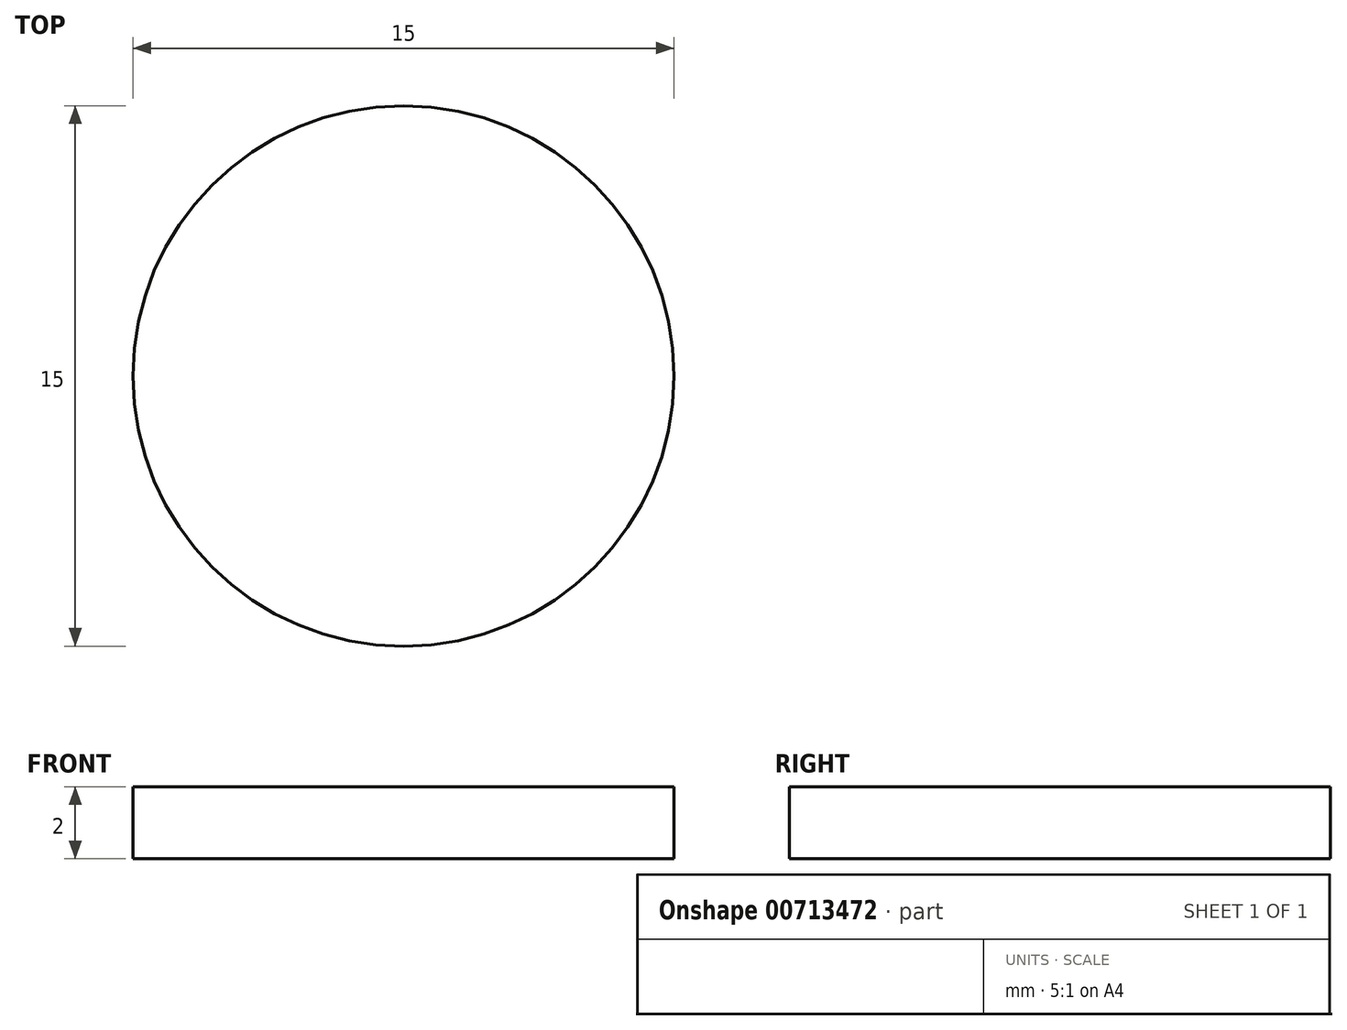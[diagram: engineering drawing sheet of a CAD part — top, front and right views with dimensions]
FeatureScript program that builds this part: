
annotation { "Feature Type Name" : "Feature", "Feature Type Description" : "" }
export const myFeature = defineFeature(function(context is Context, id is Id, definition is map)
    precondition{}
    {
        {
            var Q0;
            Q0=qCreatedBy(makeId("Top.planeOp"),FACE);
            var sketch = newSketch(context, id + "F0", { "sketchPlane" : qUnion([Q0])});
            skCircle(sketch, "E0", {"center": v(0, 0) * mm, "radius": 7.5 * mm});
            skSolve(sketch);
        }
        {
            var Q0;
            Q0 = qSketchRegion(id + "F0", true);
            extrude(context, id + "F1", {"entities" : qUnion([Q0]), "depth" : 2 * mm, "offsetDistance" : 25 * mm});
        }
    });
